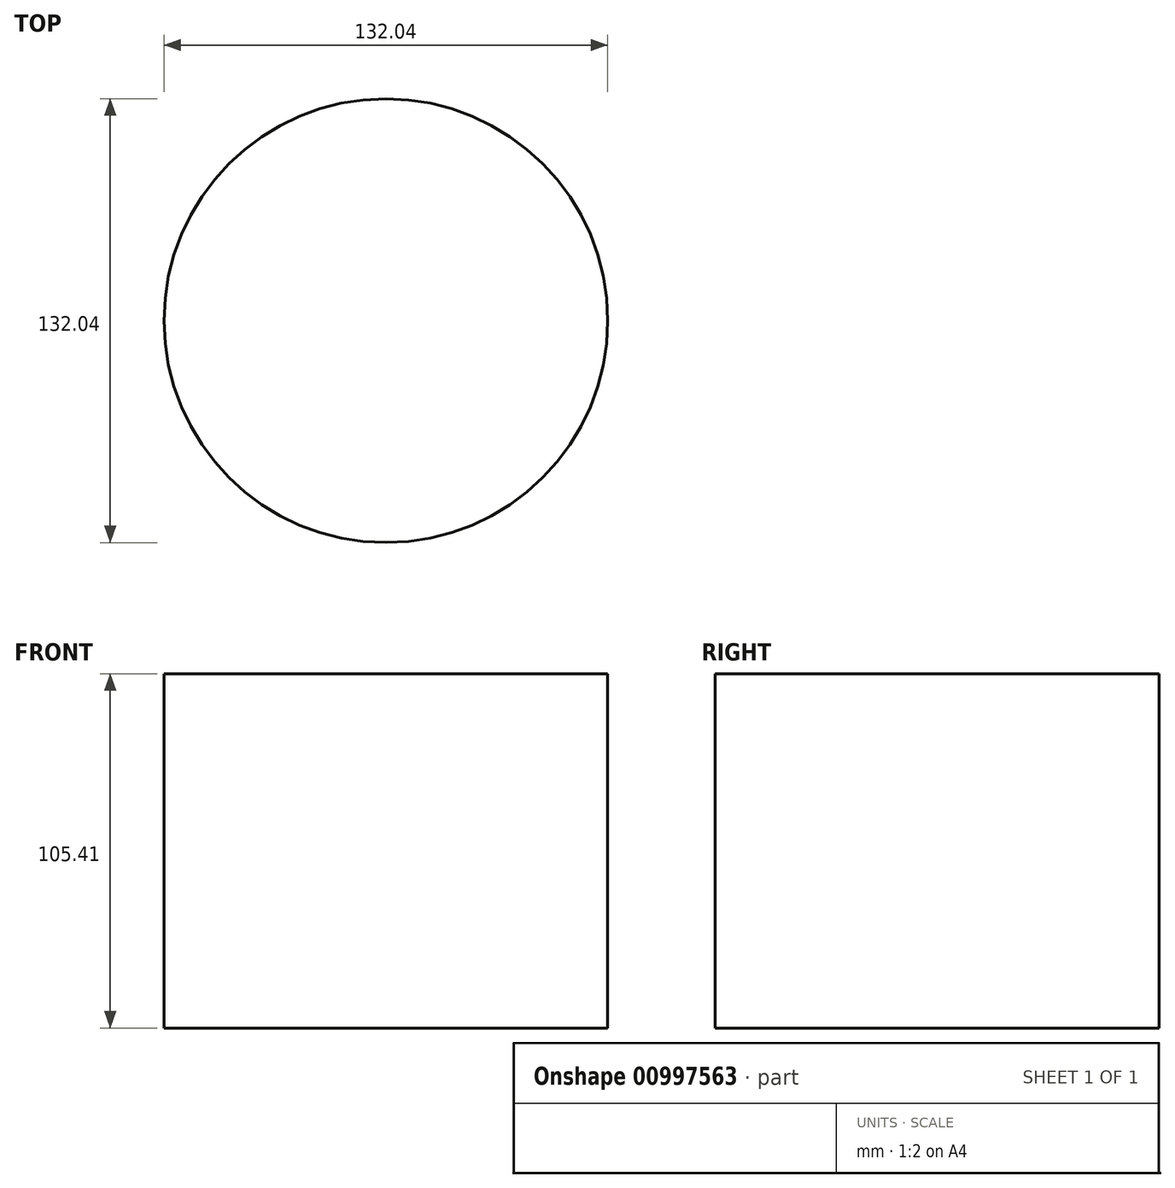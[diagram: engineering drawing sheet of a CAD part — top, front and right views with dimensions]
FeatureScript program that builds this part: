
annotation { "Feature Type Name" : "Feature", "Feature Type Description" : "" }
export const myFeature = defineFeature(function(context is Context, id is Id, definition is map)
    precondition{}
    {
        {
            var Q0;
            Q0=qCreatedBy(makeId("Top.planeOp"),FACE);
            var sketch = newSketch(context, id + "F0", { "sketchPlane" : qUnion([Q0])});
            skCircle(sketch, "E0", {"center": v(0, 0) * mm, "radius": 66.02 * mm});
            skSolve(sketch);
        }
        {
            var Q0;
            Q0=sQuery(id+"F0.wireOp",EDGE,"E0");
            extrude(context, id + "F1", {"bodyType" : ToolBodyType.SURFACE, "surfaceEntities" : qUnion([Q0]), "depth" : 105.4 * mm, "offsetDistance" : 25.4 * mm});
        }
    });
